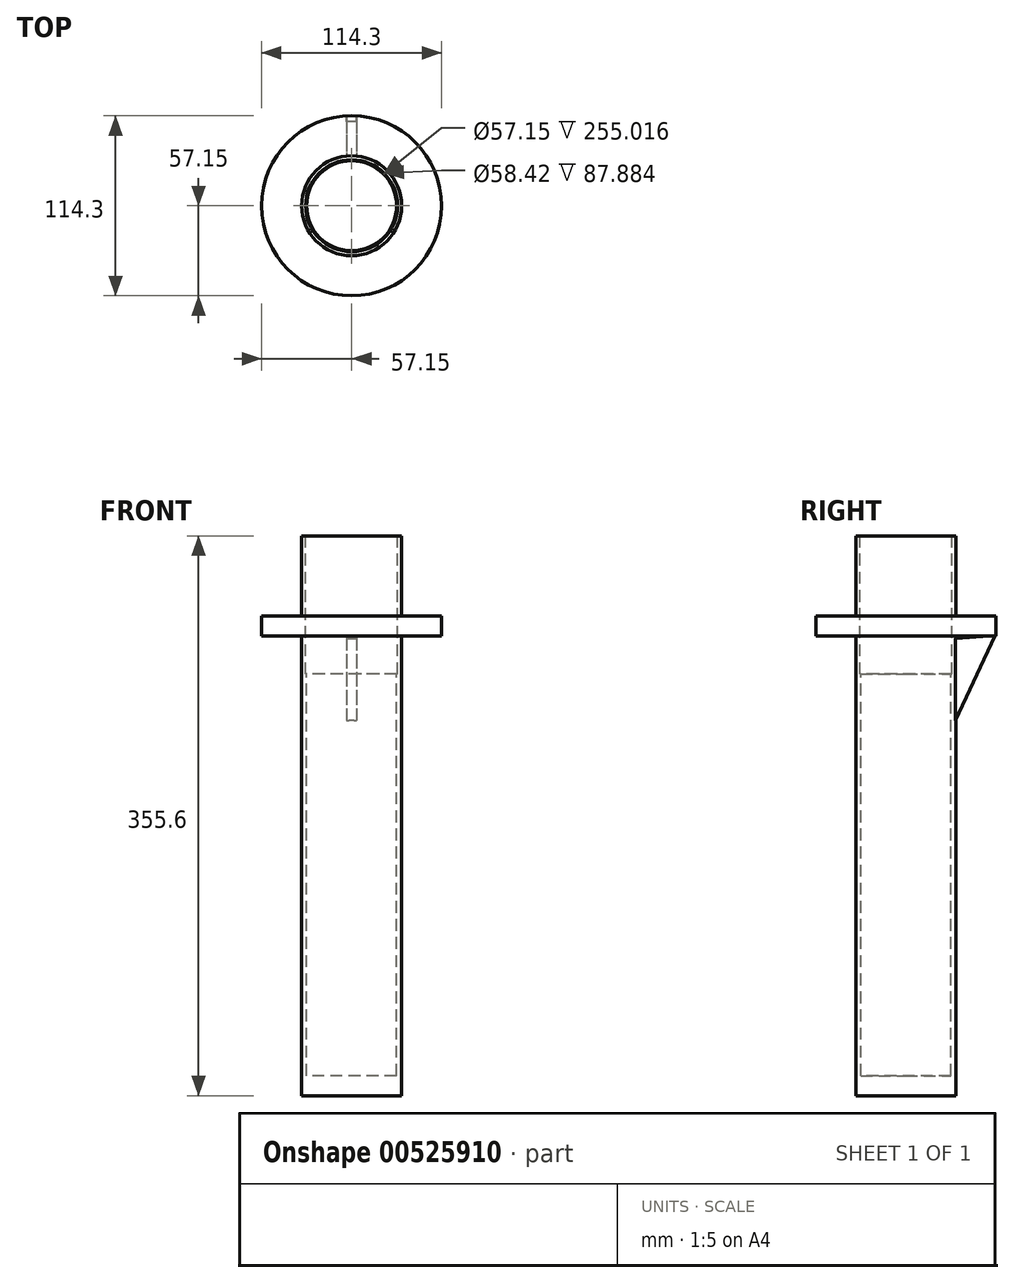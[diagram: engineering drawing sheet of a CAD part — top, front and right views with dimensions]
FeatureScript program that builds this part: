
annotation { "Feature Type Name" : "Feature", "Feature Type Description" : "" }
export const myFeature = defineFeature(function(context is Context, id is Id, definition is map)
    precondition{}
    {
        {
            var Q0;
            Q0=qCreatedBy(makeId("Top.planeOp"),FACE);
            var sketch = newSketch(context, id + "F0", { "sketchPlane" : qUnion([Q0])});
            skCircle(sketch, "E0", {"center": v(0, 0) * mm, "radius": 31.75 * mm});
            skSolve(sketch);
        }
        {
            var Q0;
            Q0 = qSketchRegion(id + "F0", true);
            extrude(context, id + "F1", {"entities" : qUnion([Q0]), "depth" : 304.8 * mm, "offsetDistance" : 25.4 * mm});
        }
        {
            var Q0;
            Q0=makeQuery(id+"F1.opExtrude","CAP_FACE",FACE,{"disambiguationData":[OSD([sQuery(id+"F0.wireOp",EDGE,"E0")])],"isStart":false});
            var sketch = newSketch(context, id + "F2", { "sketchPlane" : qUnion([Q0])});
            skCircle(sketch, "E1", {"center": v(0, 0) * mm, "radius": 28.57 * mm});
            skSolve(sketch);
        }
        {
            var Q0;
            Q0 = qSketchRegion(id + "F2", true);
            extrude(context, id + "F3", {"entities" : qUnion([Q0]), "operationType" : NewBodyOperationType.REMOVE, "oppositeDirection" : true, "depth" : 292.1 * mm, "offsetDistance" : 25.4 * mm});
        }
        {
            var Q0;
            Q0=makeQuery(id+"F1.opExtrude","CAP_FACE",FACE,{"disambiguationData":[OSD([sQuery(id+"F0.wireOp",EDGE,"E0")])],"isStart":false});
            var sketch = newSketch(context, id + "F4", { "sketchPlane" : qUnion([Q0])});
            skCircle(sketch, "E2", {"center": v(0, 0) * mm, "radius": 57.15 * mm});
            skSolve(sketch);
        }
        {
            var Q0;
            Q0=makeQuery(id+"F4.imprint","IMPRINT",FACE,{"disambiguationData":[TD([[makeQuery(id+"F4.imprint","IMPRINT",EDGE,{"derivedFrom":sQuery(id+"F4.wireOp",EDGE,"E2")}),1.0]])]});
            var Q1;
            Q1=sQuery(id+"F4.wireOp",EDGE,"E2");
            extrude(context, id + "F5", {"entities" : qUnion([Q0]), "operationType" : NewBodyOperationType.ADD, "surfaceEntities" : qUnion([Q1]), "oppositeDirection" : true, "depth" : 12.7 * mm, "offsetDistance" : 25.4 * mm});
        }
        {
            var Q0;
            Q0=qCreatedBy(makeId("Right.planeOp"),FACE);
            var sketch = newSketch(context, id + "F6", { "sketchPlane" : qUnion([Q0])});
            skLineSegment(sketch, "E3", {"start": v(56.9, 292.4) * mm, "end": v(30.9, 236.74) * mm});
            skLineSegment(sketch, "E4", {"start": v(30.9, 236.74) * mm, "end": v(30.9, 290.25) * mm});
            skLineSegment(sketch, "E5", {"start": v(56.9, 292.4) * mm, "end": v(30.9, 290.25) * mm});
            skSolve(sketch);
        }
        {
            var Q0;
            Q0=makeQuery(id+"F6.imprint","IMPRINT",FACE,{"disambiguationData":[TD([[makeQuery(id+"F6.imprint","IMPRINT",EDGE,{"derivedFrom":sQuery(id+"F6.wireOp",EDGE,"E3")}),-1.0]])]});
            extrude(context, id + "F7", {"entities" : qUnion([Q0]), "operationType" : NewBodyOperationType.ADD, "endBound" : BoundingType.SYMMETRIC, "depth" : 6.35 * mm, "offsetDistance" : 25.4 * mm});
        }
        {
            var Q0;
            {var subQ0=sQuery(id+"F0.wireOp",EDGE,"E0");Q0=makeQuery(id+"F5.boolean.opBoolean","MERGE",FACE,{"derivedFrom":[makeQuery(id+"F1.opExtrude","CAP_FACE",FACE,{"disambiguationData":[OSD([subQ0])],"isStart":false}),makeQuery(id+"F5.opExtrude","CAP_FACE",FACE,{"disambiguationData":[OSD([subQ0,sQuery(id+"F4.wireOp",EDGE,"E2")])],"isStart":true})]});}
            var sketch = newSketch(context, id + "F8", { "sketchPlane" : qUnion([Q0])});
            skCircle(sketch, "E6", {"center": v(0, 0) * mm, "radius": 31.75 * mm});
            skSolve(sketch);
        }
        {
            var Q0;
            Q0 = qSketchRegion(id + "F8", true);
            extrude(context, id + "F9", {"entities" : qUnion([Q0]), "operationType" : NewBodyOperationType.ADD, "depth" : 50.8 * mm, "offsetDistance" : 25.4 * mm});
        }
        {
            var Q0;
            Q0=makeQuery(id+"F9.opExtrude","CAP_FACE",FACE,{"disambiguationData":[OSD([sQuery(id+"F8.wireOp",EDGE,"E6")])],"isStart":false});
            var sketch = newSketch(context, id + "F10", { "sketchPlane" : qUnion([Q0])});
            skCircle(sketch, "E7", {"center": v(0, 0) * mm, "radius": 29.2 * mm});
            skSolve(sketch);
        }
        {
            var Q0;
            Q0 = qSketchRegion(id + "F10", true);
            extrude(context, id + "F11", {"entities" : qUnion([Q0]), "operationType" : NewBodyOperationType.REMOVE, "oppositeDirection" : true, "depth" : 87.88 * mm, "offsetDistance" : 25.4 * mm});
        }
    });
